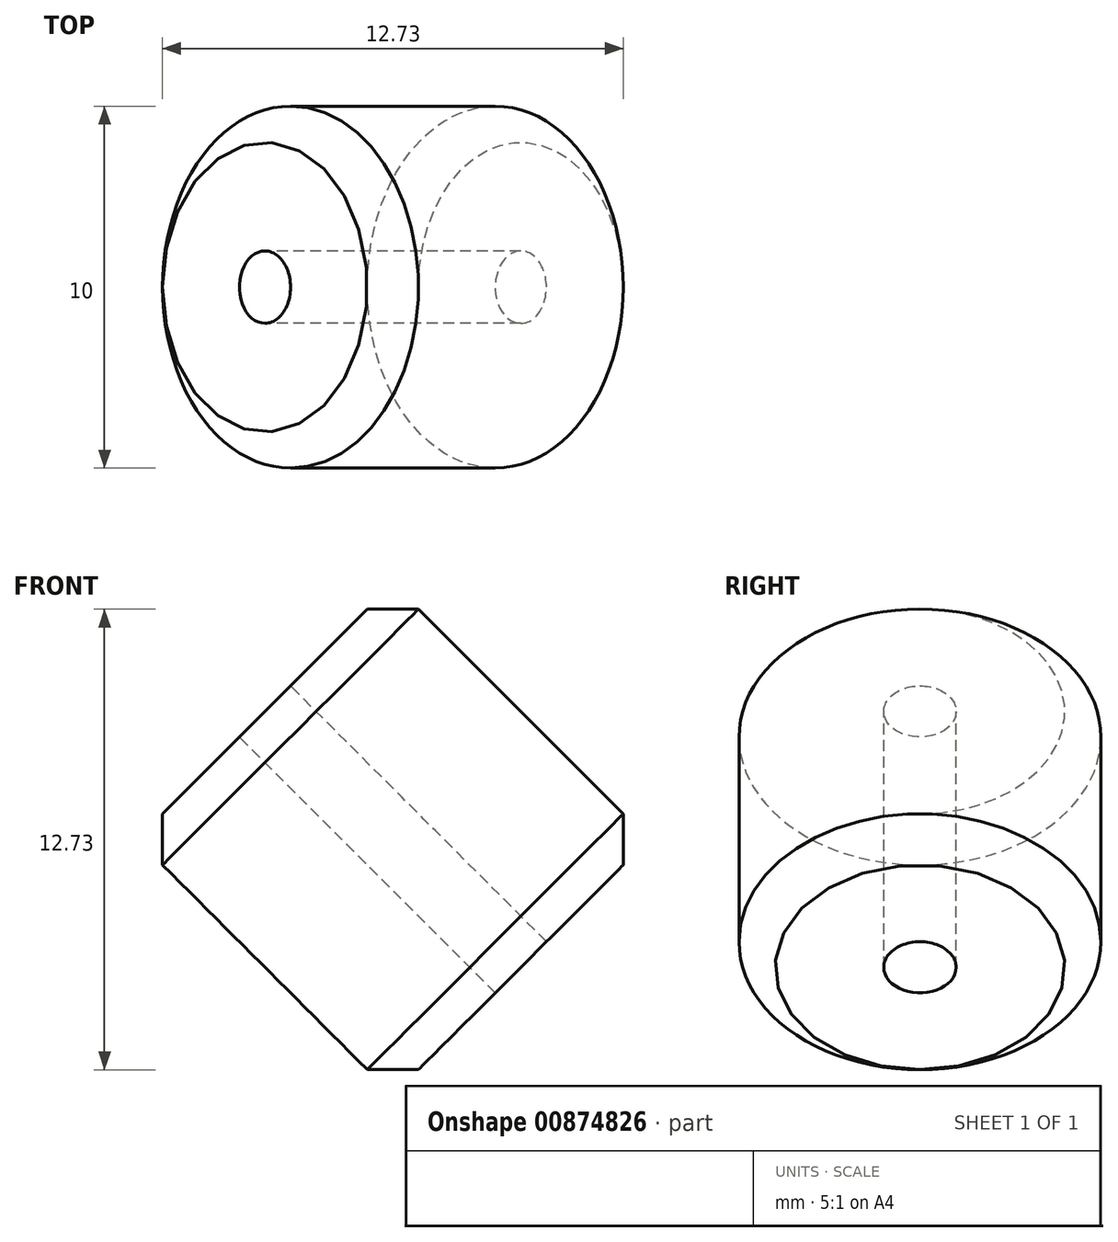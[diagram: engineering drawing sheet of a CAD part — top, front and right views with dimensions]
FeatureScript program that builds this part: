
annotation { "Feature Type Name" : "Feature", "Feature Type Description" : "" }
export const myFeature = defineFeature(function(context is Context, id is Id, definition is map)
    precondition{}
    {
        {
            var Q0;
            Q0=qCreatedBy(makeId("Front.planeOp"),FACE);
            var sketch = newSketch(context, id + "F0", { "sketchPlane" : qUnion([Q0])});
            skPoint(sketch, "E0.endSnap0", {"position": v(-14.28, 7.14) * mm});
            skLineSegment(sketch, "E1", {"start": v(0, 0) * mm, "end": v(-7.14, 7.14) * mm});
            skPoint(sketch, "E2.endSnap0", {"position": v(0, 7.14) * mm});
            skPoint(sketch, "E3.orphan", {"position": v(-14.28, 14.28) * mm});
            skPoint(sketch, "E4.right.start.orphan", {"position": v(-14.28, 0) * mm});
            skPoint(sketch, "E4.bottom.end.orphan", {"position": v(-7.14, 0) * mm});
            skLineSegment(sketch, "E5", {"start": v(0, 0) * mm, "end": v(0, -2) * mm});
            skLineSegment(sketch, "E6", {"start": v(-7.14, 7.14) * mm, "end": v(-12.14, 7.14) * mm});
            skLineSegment(sketch, "E7", {"start": v(0, -2) * mm, "end": v(-12.14, -2) * mm});
            skLineSegment(sketch, "E8", {"start": v(-12.14, -2) * mm, "end": v(-12.14, 7.14) * mm});
            skPoint(sketch, "E9.end.orphan", {"position": v(15, 7.14) * mm});
            skPoint(sketch, "E9.start.orphan", {"position": v(7.14, 7.14) * mm});
            skPoint(sketch, "E10.end.orphan", {"position": v(15, -2) * mm});
            skPoint(sketch, "E11.end.orphan", {"position": v(0, 14.28) * mm});
            skPoint(sketch, "E11.start.orphan", {"position": v(-9.64, 14.28) * mm});
            skLineSegment(sketch, "E12", {"start": v(15, -2) * mm, "end": v(15, 7.14) * mm});
            skLineSegment(sketch, "E13", {"start": v(-12.14, 7.14) * mm, "end": v(-11.14, 7.14) * mm});
            skLineSegment(sketch, "E14", {"start": v(-11.14, 7.14) * mm, "end": v(-9.14, 7.14) * mm});
            skLineSegment(sketch, "E15", {"start": v(-9.14, 7.14) * mm, "end": v(-7.14, 7.14) * mm});
            skLineSegment(sketch, "E16", {"start": v(-11.14, 7.14) * mm, "end": v(-11.14, 6.14) * mm});
            skLineSegment(sketch, "E17", {"start": v(-11.14, 6.14) * mm, "end": v(-9.14, 6.14) * mm});
            skLineSegment(sketch, "E18", {"start": v(-9.14, 6.14) * mm, "end": v(-9.14, 7.14) * mm});
            skLineSegment(sketch, "E19", {"start": v(-3.57, 3.57) * mm, "end": v(-3.5, 3.64) * mm});
            skLineSegment(sketch, "E20", {"start": v(-3.5, 3.64) * mm, "end": v(-7.04, 7.18) * mm});
            skLineSegment(sketch, "E21", {"start": v(-3.5, 3.64) * mm, "end": v(0.04, 0.1) * mm});
            skLineSegment(sketch, "E22", {"start": v(-7.04, 7.18) * mm, "end": v(-4.2, 10) * mm});
            skLineSegment(sketch, "E23", {"start": v(-4.2, 10) * mm, "end": v(-3.5, 10.71) * mm});
            skLineSegment(sketch, "E24", {"start": v(0.04, 0.1) * mm, "end": v(2.86, 2.93) * mm});
            skLineSegment(sketch, "E25", {"start": v(-4.2, 10) * mm, "end": v(2.86, 2.93) * mm});
            skLineSegment(sketch, "E26", {"start": v(-3.5, 10.71) * mm, "end": v(-1.3, 8.52) * mm});
            skSolve(sketch);
        }
        {
            var Q0;
            Q0=makeQuery(id+"F0.imprint","IMPRINT",FACE,{"disambiguationData":[TD([[makeQuery(id+"F0.imprint","IMPRINT",EDGE,{"derivedFrom":sQuery(id+"F0.wireOp",EDGE,"E20")}),-1.0]])]});
            var Q1;
            Q1=sQuery(id+"F0.wireOp",EDGE,"E26");
            revolve(context, id + "F1", {"surfaceOperationType" : NewSurfaceOperationType.NEW, "entities" : qUnion([Q0]), "axis" : qUnion([Q1]), "revolveType" : RevolveType.FULL});
        }
        {
            var Q0;
            Q0=makeQuery(id+"F1.opRevolve","SWEPT_EDGE",EDGE,{"disambiguationData":[OSD([sQuery(id+"F0.wireOp",EDGE,"E20"),sQuery(id+"F0.wireOp",EDGE,"E22")])]});
            var Q1;
            Q1=makeQuery(id+"F1.opRevolve","SWEPT_EDGE",EDGE,{"disambiguationData":[OSD([sQuery(id+"F0.wireOp",EDGE,"E21"),sQuery(id+"F0.wireOp",EDGE,"E24")])]});
            chamfer(context, id + "F2", {"entities" : qUnion([Q0, Q1]), "width" : 1 * mm, "tangentPropagation" : true});
        }
    });
